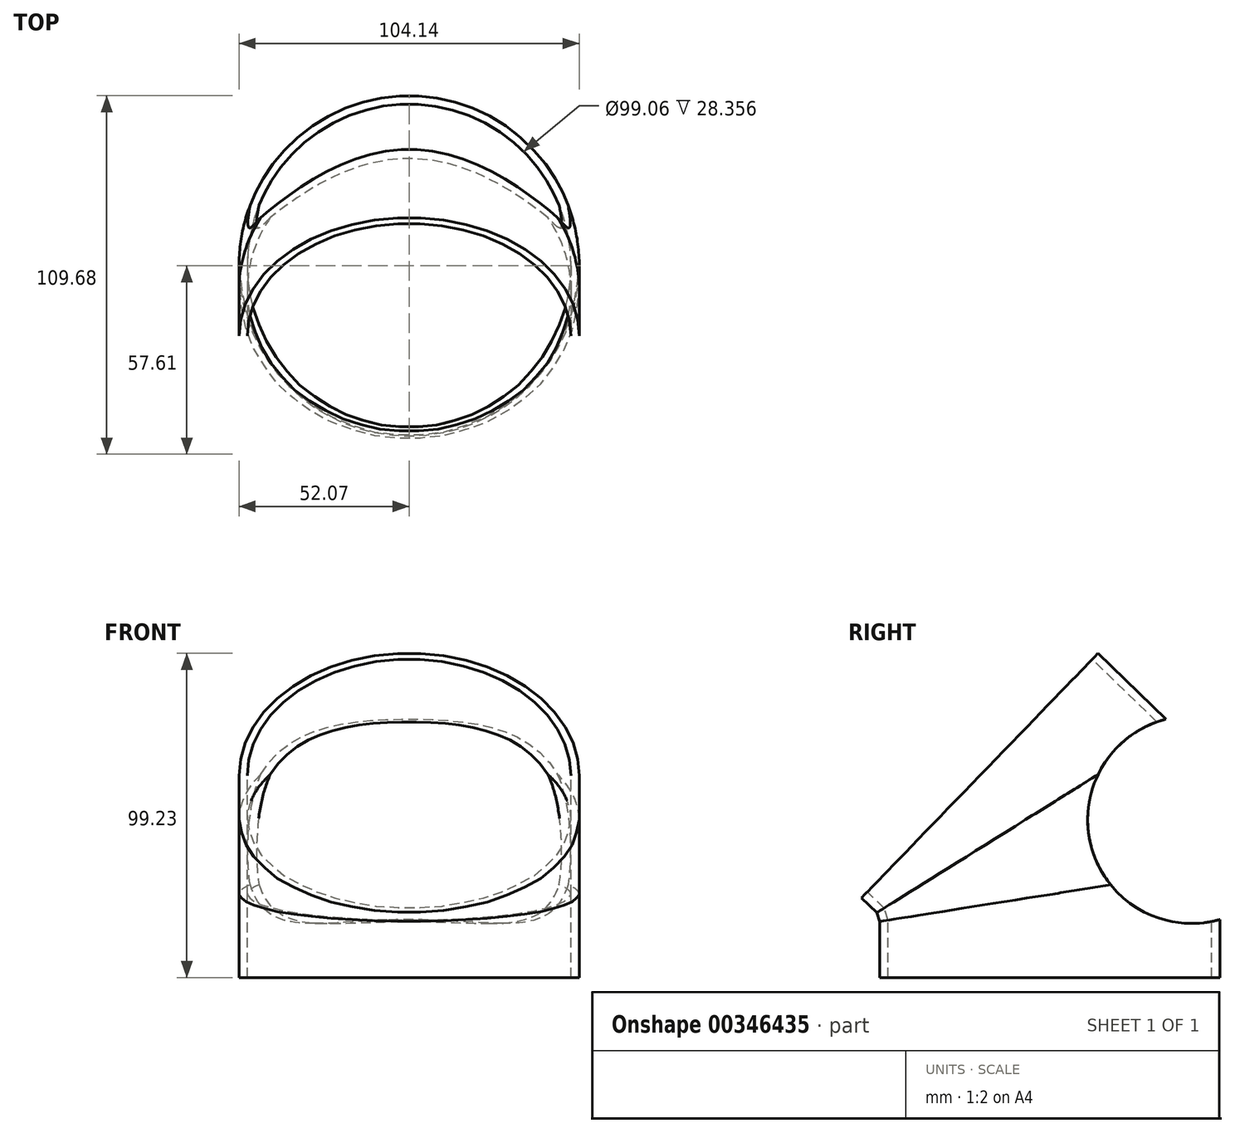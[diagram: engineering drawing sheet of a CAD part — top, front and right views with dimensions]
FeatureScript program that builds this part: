
annotation { "Feature Type Name" : "Feature", "Feature Type Description" : "" }
export const myFeature = defineFeature(function(context is Context, id is Id, definition is map)
    precondition{}
    {
        {
            var Q0;
            Q0=qCreatedBy(makeId("Top.planeOp"),FACE);
            var sketch = newSketch(context, id + "F0", { "sketchPlane" : qUnion([Q0])});
            skCircle(sketch, "E0", {"center": v(0, 0) * mm, "radius": 52.07 * mm});
            skCircle(sketch, "E1", {"center": v(0, 0) * mm, "radius": 49.53 * mm});
            skSolve(sketch);
        }
        {
            var Q0;
            Q0=qCreatedBy(makeId("Right.planeOp"),FACE);
            var sketch = newSketch(context, id + "F1", { "sketchPlane" : qUnion([Q0])});
            skLineSegment(sketch, "E2", {"start": v(0, 0) * mm, "end": v(0, 25.4) * mm});
            skLineSegment(sketch, "E3", {"start": v(0, 25.4) * mm, "end": v(-7.44, 48.28) * mm});
            skLineSegment(sketch, "E4", {"start": v(-7.44, 48.28) * mm, "end": v(-21.42, 61.8) * mm});
            skLineSegment(sketch, "E5", {"start": v(-21.42, 61.8) * mm, "end": v(-46.87, 73.27) * mm});
            skSolve(sketch);
        }
        {
            var Q0;
            Q0=makeQuery(id+"F0.imprint","IMPRINT",FACE,{"disambiguationData":[TD([[makeQuery(id+"F0.imprint","IMPRINT",EDGE,{"derivedFrom":sQuery(id+"F0.wireOp",EDGE,"E0")}),1.0]])]});
            var Q1;
            Q1=sQuery(id+"F1.wireOp",EDGE,"E2");
            var Q2;
            Q2=sQuery(id+"F1.wireOp",EDGE,"E3");
            var Q3;
            Q3=sQuery(id+"F1.wireOp",EDGE,"E4");
            sweep(context, id + "F2", {"profiles" : qUnion([Q0]), "path" : qUnion([Q1, Q2, Q3])});
        }
        {
            var Q0;
            Q0=qCreatedBy(makeId("Right.planeOp"),FACE);
            var sketch = newSketch(context, id + "F3", { "sketchPlane" : qUnion([Q0])});
            skLineSegment(sketch, "E6.0", {"start": v(0, 25.4) * mm, "end": v(-7.44, 48.28) * mm});
            skLineSegment(sketch, "E7", {"start": v(-7.44, 48.28) * mm, "end": v(43.36, 48.28) * mm});
            skCircle(sketch, "E8", {"center": v(43.36, 48.28) * mm, "radius": 31.75 * mm});
            skSolve(sketch);
        }
        {
            var Q0;
            Q0=makeQuery(id+"F3.imprint","IMPRINT",FACE,{"disambiguationData":[TD([[makeQuery(id+"F3.imprint","IMPRINT",EDGE,{"derivedFrom":sQuery(id+"F3.wireOp",EDGE,"E8")}),1.0]])]});
            extrude(context, id + "F4", {"entities" : qUnion([Q0]), "operationType" : NewBodyOperationType.REMOVE, "oppositeDirection" : true, "depth" : 50.8 * mm, "offsetDistance" : 25.4 * mm, "hasSecondDirection" : true, "secondDirectionOppositeDirection" : false, "secondDirectionDepth" : 50.8 * mm});
        }
    });
